# Revit family: S-tank_SSCT
name_source: partatom
category: Оборудование
units: mm (PartAtom-declared; Revit-internal decimal feet)

## family parameters
Всегда вертикально = Да
Классификация = Нет
На основе рабочей плоскости = Нет
Общий = Нет
При загрузке вырезать с полостями = Нет
Размер круглого соединителя = Использовать диаметр
Тип детали = Нормальный
Точка расчета площади = Нет

## types (9) — shared parameters
ADSK_URL документации изделия = http://s-tank.ru
ADSK_Группирование = Оборудование
ADSK_Единица измерения = шт.
ADSK_Завод-изготовитель = ООО “С-ТЭНК ВОТЕР ХИТЕРС”
ADSK_Наименование = Холодоаккумулятор
DN2 = 15 мм
H4 = 185 мм
Reflex_item_color = <По категории>
VLeg_b = Да
VLeg_s = Нет
shrf = 18 мм
v = 50 мм
Разработка семейств = https://rubim.tech

## per-type parameters (varying)
| type | A | ADSK_Код изделия | ADSK_Марка | ADSK_Масса | B | C | DN1 | E | H | a | Диаметрсизоляцией |
| SSCT300 | 125 мм | 2.9001 | SSCT 300 | 65 | 260 мм | 1310 мм | 25 мм | 180 мм | 1565 мм | 90 мм | 540 мм |
| SSCT500 | 122 мм | 2.9002 | SSCT 500 | 87 | 255 мм | 1305 мм | 25 мм | 230 мм | 1565 мм | 115 мм | 690 мм |
| SSCT750 | 117 мм | 2.9003 | SSCT 750 | 130 | 245 мм | 1295 мм | 25 мм | 277 мм | 1590 мм | 138 мм | 830 мм |
| SSCT1000 | 117 мм | 2.9004 | SSCT 1000 | 131 | 245 мм | 1870 мм | 25 мм | 277 мм | 2165 мм | 138 мм | 830 мм |
| SSCT1200 | 177 мм | 2.9005 | SSCT 1200 | 174 | 315 мм | 1615 мм | 25 мм | 330 мм | 1980 мм | 165 мм | 990 мм |
| SSCT1500 | 177 мм | 2.9006 | SSCT 1500 | 200 | 315 мм | 1965 мм | 25 мм | 330 мм | 2330 мм | 165 мм | 990 мм |
| SSCT2000 | 250 мм | 2.9007 | SSCT 2000 | 246 | 400 мм | 1700 мм | 25 мм | 420 мм | 2070 мм | 210 мм | 1260 мм |
| SSCT3000 | 290 мм | 2.9008 | SSCT 3000 | 450 | 430 мм | 1730 мм | 25 мм | 550 мм | 2210 мм | 275 мм | 1650 мм |
| SSCT5000 | 290 мм | 2.9009 | SSCT 5000 | 615 | 430 мм | 2480 мм | 80 мм | 550 мм | 3010 мм | 275 мм | 1650 мм |

## geometry (parser evidence)
native form markers: Extrusion x2, Sweep x3
no freeform markers — native parametric forms only
